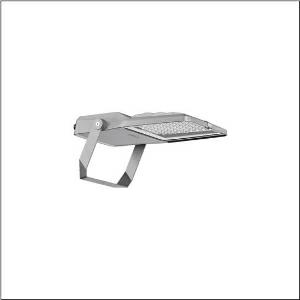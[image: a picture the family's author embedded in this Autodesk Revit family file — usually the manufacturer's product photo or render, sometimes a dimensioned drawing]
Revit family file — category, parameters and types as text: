
# Revit family: floodlight_fl_21_mini___pl64_5xa7775d2e1a_23e2
name_source: partatom
category: Lighting Fixtures
units: mm (PartAtom-declared; Revit-internal decimal feet)

## family parameters
Cut with Voids When Loaded = No
Host = Face
Light Source = No
Part Type = Normal
Room Calculation Point = No
Round Connector Dimension = Use Diameter
Shared = No

## types (1)
- --- (1 x LED, 17220 lm, 142.9 W, 3000K)
    Apparent Load = 143 VA
    CIE Flux Codes = 28 80 98 100 100
    Color Rendering = 70
    Color Temperature = 3000K
    Default Elevation = 1800 mm
    Description = Floodlight FL 21 mini, floodlight, primary light control with lens, of PMMA, primary optical cover: protective disc, of toughened safety glass, transparent, light distribution: PL64, light emission: direct distribution, installation type: surface-mounted, LED, High Power LED, rated luminous flux: 17.220lm, luminous efficacy: 121lm/W, light colour: 730, colour temperature: 3000K, control gear: Smart Interface (Zhaga), control: flexible luminous flux parameterisation, time-dependent luminous flux control, constant luminous flux control, overheat protection, pre-setting: logarithmic dimming characteristic, with terminal, 6-pole, mains connection: 220..240V, AC, 50/60Hz, start of lifetime: 143W, end of service life: 151W, reduction: 63W, luminaire housing, of diecast aluminium, powder-coated, SITECO metallic grey (DB 702S), corrosivity category C5 mid according to DIN EN ISO 12944, suitable for swimming pools, chlorine-resistant, sealing non-destructively replaceable, mounting bracket, of steel, galvanised, powder-coated, SITECO metallic grey (DB 702S), Smart Interface above, protection rating (complete): IP66, insulation class (complete): insulation class II (safety insulation), certification: CE, ENEC, VDE, protection symbol: D, impact resistance: IK08, permissible operating ambient temperature: -40..+40°C, permissible operating ambient temperature for outdoor applications: -40..+50°C, standard: DIN EN 12944, LABS conformity tested according to VDMA 24364:2018-05, packaging unit: 1 piece

Light Distribution: PL64
    Height = 70 mm
    Lamp = 1 x LED
    Lamp Light Flux = 17220 lm
    Lamp Power = 142.9 W
    Lamp count = 1
    Length = 485 mm
    Luminous efficacy = 121 lm/W
    Manufacturer = Siteco
    ModVariant = No
    Model = 5XA7775D2E1A
    Number of Poles = 1
    OnlyDefault = Yes
    Power Factor = 1
    Product Name = Floodlight FL 21 mini | PL64
    Product group = floodlight | pylon annexe
    ProductGroupID = 6201
    Protection Class = Protection class II
    Protection Degree = IP 66
    RLX_Detail_Level = 1
    RLX_Emergency_Light_Flux = 0 lm
    RLX_Emergency_Type = 0
    RLX_Emergency_Type_DB = No
    RlxData = <blob elided: 96317 chars, md5=8719b0fe>
    Socket = socket
    Standby Power = 0 W
    System Light Flux = 17220 lm
    System Power = 143 W
    Type Comments = factory setting: luminous flux: 100 % | dim-lin: 254 | 730 mA
    Type Image = l_1006845.jpg
    URL = http://relux.com
    VarID = @adj_164781
    Voltage = 0 V
    Weight = 0.00 kg
    Width = 337 mm

## geometry (parser evidence)
native form markers: Blend x4, Sweep x12
no freeform markers — native parametric forms only
